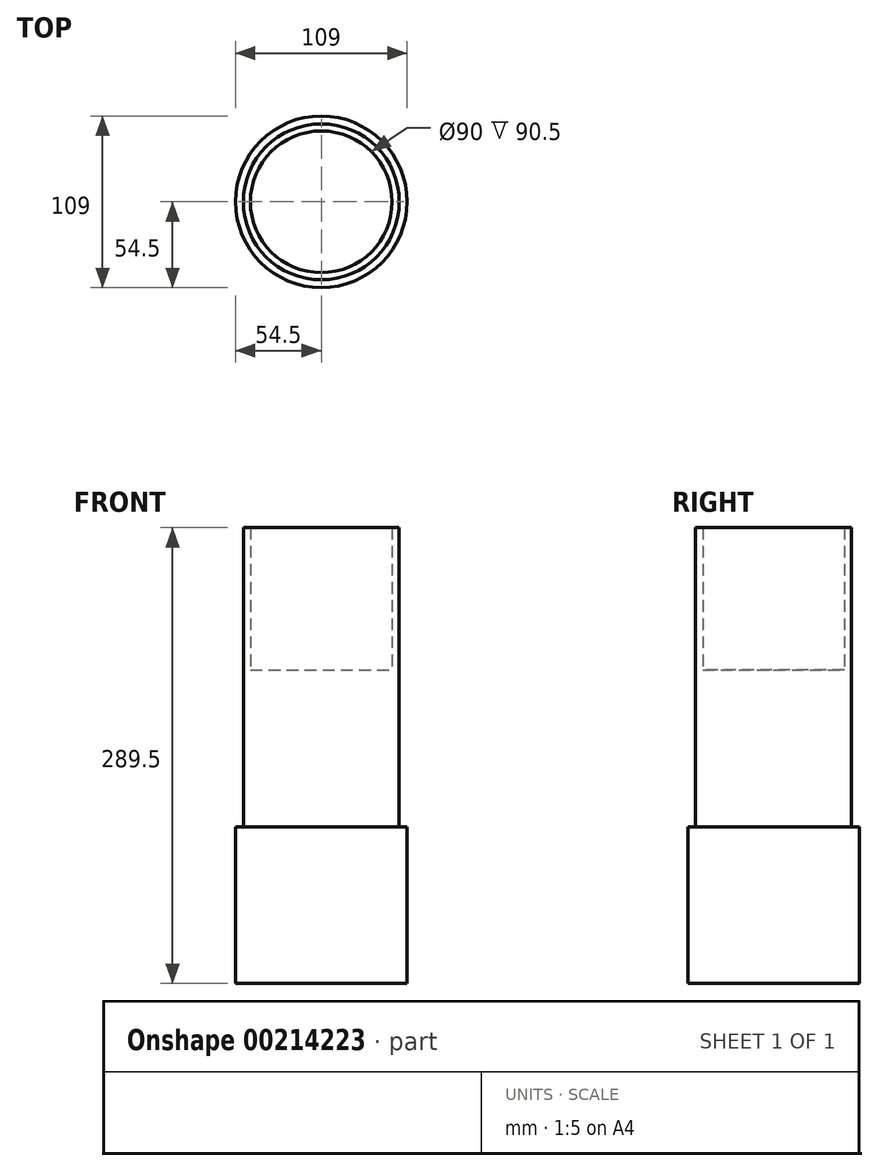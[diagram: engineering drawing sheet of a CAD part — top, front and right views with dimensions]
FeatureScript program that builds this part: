
annotation { "Feature Type Name" : "Feature", "Feature Type Description" : "" }
export const myFeature = defineFeature(function(context is Context, id is Id, definition is map)
    precondition{}
    {
        {
            var Q0;
            Q0=qCreatedBy(makeId("Front.planeOp"),FACE);
            var sketch = newSketch(context, id + "F0", { "sketchPlane" : qUnion([Q0])});
            skLineSegment(sketch, "E0", {"start": v(0, 0) * mm, "end": v(0, 0) * mm});
            skLineSegment(sketch, "E1.bottom", {"start": v(-1.68, 0) * mm, "end": v(54.5, 0) * mm});
            skLineSegment(sketch, "E1.top", {"start": v(49.5, 99.5) * mm, "end": v(54.5, 99.5) * mm});
            skLineSegment(sketch, "E1.right", {"start": v(54.5, 0) * mm, "end": v(54.5, 99.5) * mm});
            skLineSegment(sketch, "E2.top", {"start": v(49.5, 199) * mm, "end": v(49.5, 199) * mm});
            skLineSegment(sketch, "E2.left", {"start": v(49.5, 99.5) * mm, "end": v(49.5, 199) * mm});
            skLineSegment(sketch, "E2.right", {"start": v(0, 0) * mm, "end": v(0, 199) * mm});
            skLineSegment(sketch, "E3.top", {"start": v(49.5, 289.5) * mm, "end": v(45, 289.5) * mm});
            skLineSegment(sketch, "E3.left", {"start": v(45, 199) * mm, "end": v(45, 289.5) * mm});
            skLineSegment(sketch, "E3.right", {"start": v(49.5, 199) * mm, "end": v(49.5, 289.5) * mm});
            skLineSegment(sketch, "E4.trimOffspring", {"start": v(45, 199) * mm, "end": v(0, 199) * mm});
            skSolve(sketch);
        }
        {
            var Q0;
            Q0=makeQuery(id+"F0.imprint","IMPRINT",FACE,{"disambiguationData":[TD([[makeQuery(id+"F0.imprint","IMPRINT",EDGE,{"derivedFrom":sQuery(id+"F0.wireOp",EDGE,"E1.top")}),-1.0]])]});
            var Q1;
            Q1=sQuery(id+"F0.wireOp",EDGE,"E2.right");
            revolve(context, id + "F1", {"entities" : qUnion([Q0]), "axis" : qUnion([Q1]), "revolveType" : RevolveType.FULL});
        }
    });
